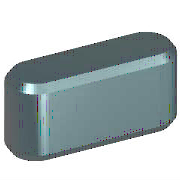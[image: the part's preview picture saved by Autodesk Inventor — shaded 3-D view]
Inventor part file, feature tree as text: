
AUTODESK INVENTOR PART (.ipt)
format: ipt  version: 2025 (Build 290162000, 162)  size: 138,240 bytes
history: native  units: mm (DEFAULTED — no unit token found)
features: plane x3, extrude x1
ambient origin geometry x8: Origin, YZ Plane, XZ Plane, XY Plane, X Axis, Y Axis, Z Axis, Center Point
bodies: Solid1 (feature_tree)
feature tree (4):
  plane  "Work Plane1"
  plane  "Work Plane2"
  extrude  "轴承体1"  Depth=6.0mm
  plane  "Work Plane3"
